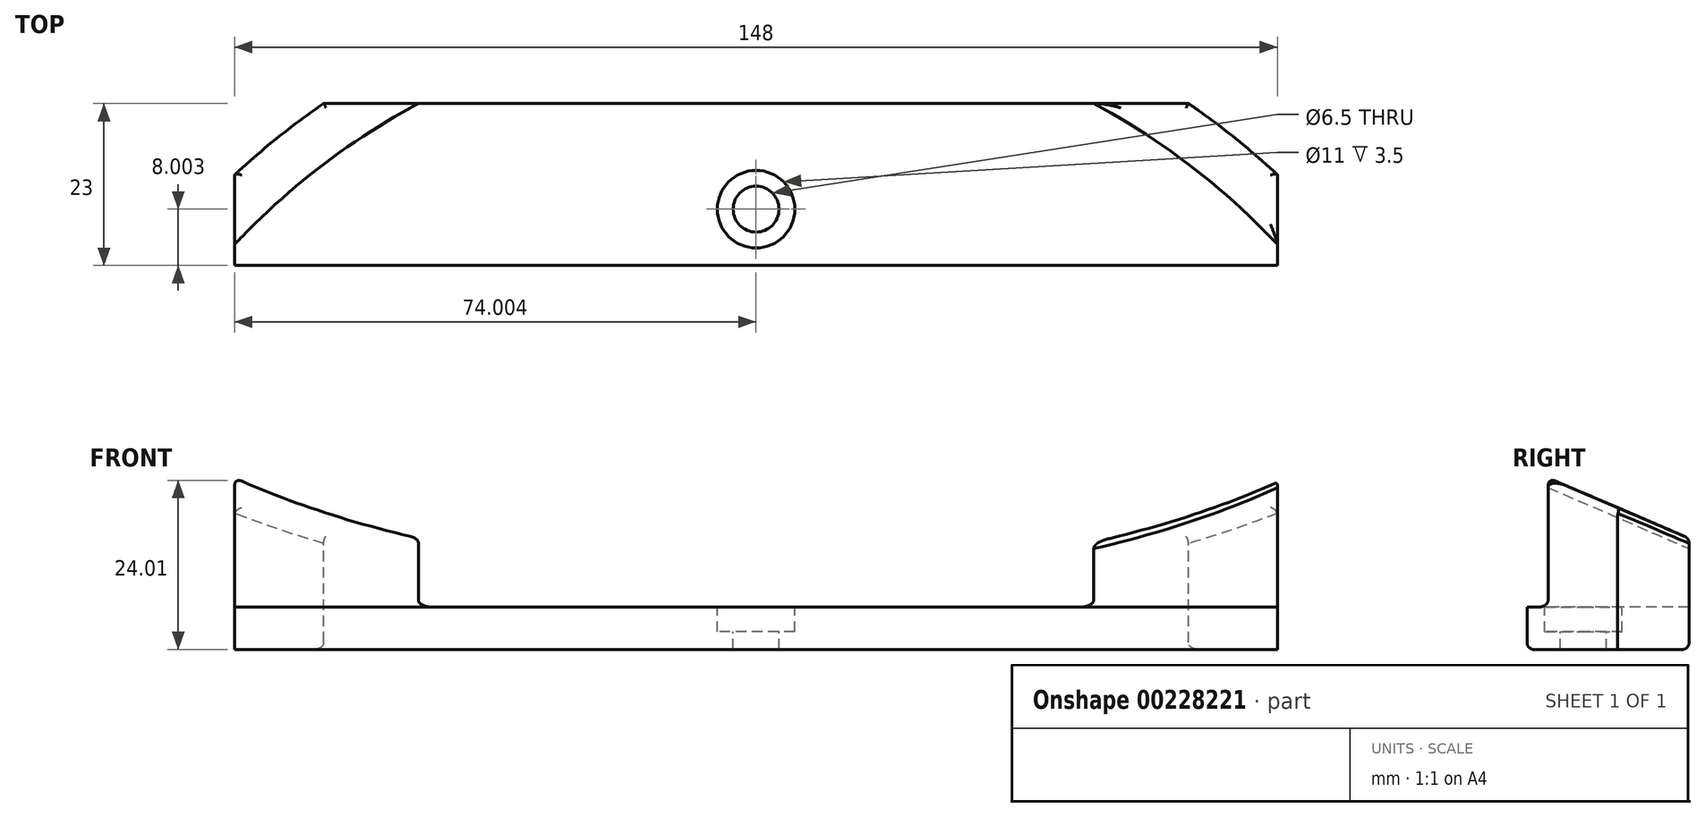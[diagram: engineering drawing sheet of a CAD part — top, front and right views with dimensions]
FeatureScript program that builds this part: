
annotation { "Feature Type Name" : "Feature", "Feature Type Description" : "" }
export const myFeature = defineFeature(function(context is Context, id is Id, definition is map)
    precondition{}
    {
        {
            var Q0;
            Q0=qCreatedBy(makeId("Top.planeOp"),FACE);
            var sketch = newSketch(context, id + "F0", { "sketchPlane" : qUnion([Q0])});
            skLineSegment(sketch, "E0.bottom", {"start": v(-72.48, -7.14) * mm, "end": v(107.52, -7.14) * mm});
            skLineSegment(sketch, "E0.top", {"start": v(-72.48, -30.14) * mm, "end": v(107.52, -30.14) * mm});
            skLineSegment(sketch, "E0.left", {"start": v(-72.48, -7.14) * mm, "end": v(-72.48, -30.14) * mm});
            skLineSegment(sketch, "E0.right", {"start": v(107.52, -7.14) * mm, "end": v(107.52, -30.14) * mm});
            skPoint(sketch, "E1", {"position": v(-64.48, -22.14) * mm});
            skPoint(sketch, "E2", {"position": v(99.52, -22.14) * mm});
            skSolve(sketch);
        }
        {
            var Q0;
            Q0=makeQuery(id+"F0.imprint","IMPRINT",FACE,{"disambiguationData":[TD([[makeQuery(id+"F0.imprint","IMPRINT",EDGE,{"derivedFrom":sQuery(id+"F0.wireOp",EDGE,"E0.bottom")}),-1.0]])]});
            extrude(context, id + "F1", {"entities" : qUnion([Q0]), "depth" : 6 * mm});
        }
        {
            var Q0;
            Q0=makeQuery(id+"F1.opExtrude","CAP_FACE",FACE,{"disambiguationData":[OSD([sQuery(id+"F0.wireOp",EDGE,"E0.bottom"),sQuery(id+"F0.wireOp",EDGE,"E0.top"),sQuery(id+"F0.wireOp",EDGE,"E0.left"),sQuery(id+"F0.wireOp",EDGE,"E0.right")])],"isStart":false});
            var sketch = newSketch(context, id + "F2", { "sketchPlane" : qUnion([Q0])});
            skPoint(sketch, "E3", {"position": v(-64.48, -22.14) * mm});
            skPoint(sketch, "E4", {"position": v(99.52, -22.14) * mm});
            skLineSegment(sketch, "E5.bottom", {"start": v(-56.48, -7.14) * mm, "end": v(91.52, -7.14) * mm});
            skLineSegment(sketch, "E5.top", {"start": v(-56.48, -30.14) * mm, "end": v(91.52, -30.14) * mm});
            skLineSegment(sketch, "E5.left", {"start": v(-56.48, -7.14) * mm, "end": v(-56.48, -30.14) * mm});
            skLineSegment(sketch, "E5.right", {"start": v(91.52, -7.14) * mm, "end": v(91.52, -30.14) * mm});
            skSolve(sketch);
        }
        {
            var Q0;
            Q0=makeQuery(id+"F2.imprint","IMPRINT",FACE,{"disambiguationData":[TD([[makeQuery(id+"F2.imprint","IMPRINT",EDGE,{"derivedFrom":sQuery(id+"F2.wireOp",EDGE,"E5.bottom")}),-1.0]])]});
            extrude(context, id + "F3", {"entities" : qUnion([Q0]), "operationType" : NewBodyOperationType.ADD, "depth" : 21 * mm});
        }
        {
            var Q0;
            Q0=makeQuery(id+"F3.opExtrude","CAP_FACE",FACE,{"disambiguationData":[OSD([sQuery(id+"F2.wireOp",EDGE,"E5.bottom"),sQuery(id+"F2.wireOp",EDGE,"E5.top"),sQuery(id+"F2.wireOp",EDGE,"E5.left"),sQuery(id+"F2.wireOp",EDGE,"E5.right")])],"isStart":false});
            var sketch = newSketch(context, id + "F4", { "sketchPlane" : qUnion([Q0])});
            skPoint(sketch, "E6", {"position": v(17.52, 2.86) * mm});
            skCircle(sketch, "E7", {"center": v(17.52, -96.6) * mm, "radius": 108.5 * mm});
            skCircle(sketch, "E8", {"center": v(17.52, -96.6) * mm, "radius": 101.5 * mm});
            skSolve(sketch);
        }
        {
            var Q0;
            {var subQ1=makeQuery(id+"F3.opExtrude","CAP_EDGE",EDGE,{"disambiguationData":[OSD([sQuery(id+"F2.wireOp",EDGE,"E5.top")])],"isStart":false});Q0=makeQuery(id+"F4.imprint","IMPRINT",FACE,{"disambiguationData":[TD([[makeQuery(id+"F4.imprint","IMPRINT",EDGE,{"derivedFrom":subQ1}),1.0]])]});}
            extrude(context, id + "F5", {"entities" : qUnion([Q0]), "operationType" : NewBodyOperationType.REMOVE, "oppositeDirection" : true, "depth" : 21 * mm});
        }
        {
            var Q0;
            {var subQ0=sQuery(id+"F4.wireOp",EDGE,"E7");var subQ1=makeQuery(id+"F3.opExtrude","CAP_EDGE",EDGE,{"disambiguationData":[OSD([sQuery(id+"F2.wireOp",EDGE,"E5.bottom")])],"isStart":false});var subQ2=makeQuery(id+"F4.imprint","INTERSECT",VERTEX,{"disambiguationData":[OD(1.0)],"derivedFrom":[subQ1,subQ0]});Q0=makeQuery(id+"F4.imprint","IMPRINT",FACE,{"disambiguationData":[TD([[makeQuery(id+"F4.imprint","IMPRINT",EDGE,{"disambiguationData":[TD([[subQ2,-1.0]])],"derivedFrom":subQ0}),-1.0]])]});}
            var Q1;
            {var subQ0=sQuery(id+"F4.wireOp",EDGE,"E7");var subQ1=makeQuery(id+"F3.opExtrude","CAP_EDGE",EDGE,{"disambiguationData":[OSD([sQuery(id+"F2.wireOp",EDGE,"E5.bottom")])],"isStart":false});var subQ2=makeQuery(id+"F4.imprint","INTERSECT",VERTEX,{"disambiguationData":[OD(0.0)],"derivedFrom":[subQ1,subQ0]});Q1=makeQuery(id+"F4.imprint","IMPRINT",FACE,{"disambiguationData":[TD([[makeQuery(id+"F4.imprint","IMPRINT",EDGE,{"disambiguationData":[TD([[subQ2,1.0]])],"derivedFrom":subQ0}),-1.0]])]});}
            extrude(context, id + "F6", {"entities" : qUnion([Q0, Q1]), "operationType" : NewBodyOperationType.REMOVE, "oppositeDirection" : true, "depth" : 35 * mm});
        }
        {
            var Q0;
            Q0=makeQuery(id+"F1.opExtrude","SWEPT_FACE",FACE,{"disambiguationData":[OSD([sQuery(id+"F0.wireOp",EDGE,"E0.right")])]});
            var sketch = newSketch(context, id + "F7", { "sketchPlane" : qUnion([Q0])});
            skLineSegment(sketch, "E9", {"start": v(-33.26, 27) * mm, "end": v(-1.82, 13.5) * mm});
            skLineSegment(sketch, "E10", {"start": v(-1.82, 13.5) * mm, "end": v(-1.82, 27.27) * mm});
            skLineSegment(sketch, "E11", {"start": v(-1.82, 27.27) * mm, "end": v(-33.26, 27) * mm});
            skSolve(sketch);
        }
        {
            var Q0;
            Q0=makeQuery(id+"F7.imprint","IMPRINT",FACE,{"disambiguationData":[TD([[makeQuery(id+"F7.imprint","IMPRINT",EDGE,{"derivedFrom":sQuery(id+"F7.wireOp",EDGE,"E9")}),1.0]])]});
            extrude(context, id + "F8", {"entities" : qUnion([Q0]), "operationType" : NewBodyOperationType.REMOVE, "oppositeDirection" : true, "depth" : 200 * mm});
        }
        {
            var Q0;
            {var subQ0=sQuery(id+"F2.wireOp",EDGE,"E5.left");Q0=makeQuery(id+"F2.imprint","IMPRINT",FACE,{"disambiguationData":[TD([[makeQuery(id+"F2.imprint","IMPRINT",EDGE,{"derivedFrom":subQ0}),-1.0]])]});}
            var Q1;
            {var subQ0=sQuery(id+"F2.wireOp",EDGE,"E5.right");Q1=makeQuery(id+"F2.imprint","IMPRINT",FACE,{"disambiguationData":[TD([[makeQuery(id+"F2.imprint","IMPRINT",EDGE,{"derivedFrom":subQ0}),1.0]])]});}
            extrude(context, id + "F9", {"entities" : qUnion([Q0, Q1]), "operationType" : NewBodyOperationType.REMOVE, "oppositeDirection" : true, "depth" : 25 * mm});
        }
        {
            var Q0;
            {var subQ0=sQuery(id+"F2.wireOp",EDGE,"E5.right");var subQ1=sQuery(id+"F2.wireOp",EDGE,"E5.left");var subQ2=sQuery(id+"F2.wireOp",EDGE,"E5.top");var subQ3=sQuery(id+"F2.wireOp",EDGE,"E5.bottom");var subQ4=sQuery(id+"F0.wireOp",EDGE,"E0.right");var subQ6=sQuery(id+"F0.wireOp",EDGE,"E0.top");var subQ8=sQuery(id+"F0.wireOp",EDGE,"E0.bottom");var subQ11=sQuery(id+"F0.wireOp",EDGE,"E0.left");var subQ12=makeQuery(id+"F1.opExtrude","CAP_FACE",FACE,{"disambiguationData":[OSD([subQ8,subQ6,subQ11,subQ4])],"isStart":false});Q0=makeQuery(id+"F5.boolean.opBoolean","MERGE",FACE,{"derivedFrom":[makeQuery(id+"F3.boolean.opBoolean","SPLIT",FACE,{"disambiguationData":[TD([makeQuery(id+"F1.opExtrude","SWEPT_FACE",FACE,{"disambiguationData":[OSD([subQ11])]})])],"derivedFrom":subQ12}),makeQuery(id+"F3.boolean.opBoolean","SPLIT",FACE,{"disambiguationData":[TD([makeQuery(id+"F1.opExtrude","SWEPT_FACE",FACE,{"disambiguationData":[OSD([subQ4])]})])],"derivedFrom":subQ12}),makeQuery(id+"F5.opExtrude","CAP_FACE",FACE,{"disambiguationData":[OSD([subQ3,subQ2,subQ1,subQ0,sQuery(id+"F4.wireOp",EDGE,"E8")])],"isStart":false})]});}
            var sketch = newSketch(context, id + "F10", { "sketchPlane" : qUnion([Q0])});
            skPoint(sketch, "E12", {"position": v(17.52, -22.14) * mm});
            skSolve(sketch);
        }
        {
            var Q0;
            Q0=sQuery(id+"F10.wireOp",VERTEX,"E12");
            var Q1;
            Q1=makeQuery(id+"F1.opExtrude","SWEPT_BODY",BODY,{"disambiguationData":[OSD([sQuery(id+"F0.wireOp",EDGE,"E0.bottom"),sQuery(id+"F0.wireOp",EDGE,"E0.top"),sQuery(id+"F0.wireOp",EDGE,"E0.left"),sQuery(id+"F0.wireOp",EDGE,"E0.right")])]});
            hole(context, id + "F11", {"style" : HoleStyle.C_BORE, "endStyle" : HoleEndStyle.THROUGH, "holeDiameter" : 6.5 * mm, "cBoreDiameter" : 11 * mm, "cBoreDepth" : 3.5 * mm, "startFromSketch" : true, "locations" : qUnion([Q0]), "scope" : qUnion([Q1]), "isTappedThrough" : true});
        }
        {
            var Q0;
            Q0=makeQuery(id+"F5.boolean.opBoolean","COPY",EDGE,{"derivedFrom":makeQuery(id+"F5.opExtrude","CAP_EDGE",EDGE,{"disambiguationData":[OSD([sQuery(id+"F2.wireOp",EDGE,"E5.bottom")])],"isStart":false})});
            var Q1;
            Q1=makeQuery(id+"F5.boolean.opBoolean","COPY",EDGE,{"derivedFrom":makeQuery(id+"F5.opExtrude","CAP_EDGE",EDGE,{"disambiguationData":[OSD([sQuery(id+"F2.wireOp",EDGE,"E5.top")])],"isStart":false})});
            var Q2;
            {var subQ0=sQuery(id+"F4.wireOp",EDGE,"E7");var subQ1=sQuery(id+"F2.wireOp",EDGE,"E5.bottom");var subQ2=makeQuery(id+"F3.opExtrude","CAP_EDGE",EDGE,{"disambiguationData":[OSD([subQ1])],"isStart":false});var subQ3=sQuery(id+"F0.wireOp",EDGE,"E0.bottom");Q2=makeQuery(id+"F6.boolean.opBoolean","SPLIT",EDGE,{"disambiguationData":[TD([makeQuery(id+"F6.opExtrude","SWEPT_FACE",FACE,{"disambiguationData":[OSD([subQ0]),TDD([makeQuery(id+"F4.imprint","IMPRINT",EDGE,{"disambiguationData":[TD([[makeQuery(id+"F4.imprint","INTERSECT",VERTEX,{"disambiguationData":[OD(0.0)],"derivedFrom":[subQ2,subQ0]}),1.0]])],"derivedFrom":subQ0})])]})])],"derivedFrom":makeQuery(id+"F1.opExtrude","CAP_EDGE",EDGE,{"disambiguationData":[OSD([subQ3])],"isStart":true})});}
            var Q3;
            Q3=makeQuery(id+"F1.opExtrude","CAP_EDGE",EDGE,{"disambiguationData":[OSD([sQuery(id+"F0.wireOp",EDGE,"E0.top")])],"isStart":true});
            var Q4;
            {var subQ0=sQuery(id+"F4.wireOp",EDGE,"E7");var subQ1=sQuery(id+"F2.wireOp",EDGE,"E5.bottom");var subQ2=sQuery(id+"F2.wireOp",EDGE,"E5.left");var subQ6=sQuery(id+"F0.wireOp",EDGE,"E0.right");var subQ7=sQuery(id+"F0.wireOp",EDGE,"E0.left");var subQ8=sQuery(id+"F0.wireOp",EDGE,"E0.top");var subQ9=sQuery(id+"F0.wireOp",EDGE,"E0.bottom");var subQ11=makeQuery(id+"F6.opExtrude","SWEPT_EDGE",EDGE,{"disambiguationData":[OSD([subQ2,subQ0])]});Q4=makeQuery(id+"F9.boolean.opBoolean","MERGE",EDGE,{"derivedFrom":[makeQuery(id+"F6.boolean.opBoolean","COPY",EDGE,{"disambiguationData":[TD([makeQuery(id+"F1.opExtrude","CAP_FACE",FACE,{"disambiguationData":[OSD([subQ9,subQ8,subQ7,subQ6])],"isStart":true})])],"derivedFrom":subQ11}),makeQuery(id+"F6.boolean.opBoolean","COPY",EDGE,{"disambiguationData":[TD([makeQuery(id+"F3.opExtrude","CAP_FACE",FACE,{"disambiguationData":[OSD([subQ1,sQuery(id+"F2.wireOp",EDGE,"E5.top"),subQ2,sQuery(id+"F2.wireOp",EDGE,"E5.right")])],"isStart":false})])],"derivedFrom":subQ11})]});}
            var Q5;
            {var subQ0=sQuery(id+"F4.wireOp",EDGE,"E7");var subQ1=sQuery(id+"F2.wireOp",EDGE,"E5.bottom");Q5=makeQuery(id+"F6.boolean.opBoolean","COPY",EDGE,{"derivedFrom":makeQuery(id+"F6.opExtrude","SWEPT_EDGE",EDGE,{"disambiguationData":[OSD([subQ1,subQ0]),TDD([makeQuery(id+"F4.imprint","INTERSECT",VERTEX,{"disambiguationData":[OD(1.0)],"derivedFrom":[makeQuery(id+"F3.opExtrude","CAP_EDGE",EDGE,{"disambiguationData":[OSD([subQ1])],"isStart":false}),subQ0]})])]})});}
            var Q6;
            {var subQ0=sQuery(id+"F4.wireOp",EDGE,"E7");var subQ1=sQuery(id+"F2.wireOp",EDGE,"E5.bottom");var subQ2=sQuery(id+"F2.wireOp",EDGE,"E5.right");var subQ5=sQuery(id+"F0.wireOp",EDGE,"E0.right");var subQ6=sQuery(id+"F0.wireOp",EDGE,"E0.left");var subQ7=sQuery(id+"F0.wireOp",EDGE,"E0.top");var subQ8=sQuery(id+"F0.wireOp",EDGE,"E0.bottom");var subQ11=makeQuery(id+"F6.opExtrude","SWEPT_EDGE",EDGE,{"disambiguationData":[OSD([subQ2,subQ0])]});Q6=makeQuery(id+"F9.boolean.opBoolean","MERGE",EDGE,{"derivedFrom":[makeQuery(id+"F6.boolean.opBoolean","COPY",EDGE,{"disambiguationData":[TD([makeQuery(id+"F1.opExtrude","CAP_FACE",FACE,{"disambiguationData":[OSD([subQ8,subQ7,subQ6,subQ5])],"isStart":true})])],"derivedFrom":subQ11}),makeQuery(id+"F6.boolean.opBoolean","COPY",EDGE,{"disambiguationData":[TD([makeQuery(id+"F3.opExtrude","CAP_FACE",FACE,{"disambiguationData":[OSD([subQ1,sQuery(id+"F2.wireOp",EDGE,"E5.top"),sQuery(id+"F2.wireOp",EDGE,"E5.left"),subQ2])],"isStart":false})])],"derivedFrom":subQ11})]});}
            var Q7;
            {var subQ0=sQuery(id+"F4.wireOp",EDGE,"E8");Q7=makeQuery(id+"F8.boolean.opBoolean","INTERSECT",EDGE,{"derivedFrom":[makeQuery(id+"F5.boolean.opBoolean","COPY",FACE,{"derivedFrom":makeQuery(id+"F5.opExtrude","SWEPT_FACE",FACE,{"disambiguationData":[OSD([subQ0]),TDD([makeQuery(id+"F4.imprint","IMPRINT",EDGE,{"disambiguationData":[TD([[makeQuery(id+"F4.imprint","INTERSECT",VERTEX,{"disambiguationData":[OD(0.0)],"derivedFrom":[makeQuery(id+"F3.opExtrude","CAP_EDGE",EDGE,{"disambiguationData":[OSD([sQuery(id+"F2.wireOp",EDGE,"E5.bottom")])],"isStart":false}),subQ0]}),1.0]])],"derivedFrom":subQ0})])]})}),makeQuery(id+"F8.opExtrude","SWEPT_FACE",FACE,{"disambiguationData":[OSD([sQuery(id+"F7.wireOp",EDGE,"E9")])]})]});}
            var Q8;
            {var subQ0=sQuery(id+"F4.wireOp",EDGE,"E7");Q8=makeQuery(id+"F8.boolean.opBoolean","INTERSECT",EDGE,{"derivedFrom":[makeQuery(id+"F6.boolean.opBoolean","COPY",FACE,{"derivedFrom":makeQuery(id+"F6.opExtrude","SWEPT_FACE",FACE,{"disambiguationData":[OSD([subQ0]),TDD([makeQuery(id+"F4.imprint","IMPRINT",EDGE,{"disambiguationData":[TD([[makeQuery(id+"F4.imprint","INTERSECT",VERTEX,{"disambiguationData":[OD(0.0)],"derivedFrom":[makeQuery(id+"F3.opExtrude","CAP_EDGE",EDGE,{"disambiguationData":[OSD([sQuery(id+"F2.wireOp",EDGE,"E5.bottom")])],"isStart":false}),subQ0]}),1.0]])],"derivedFrom":subQ0})])]})}),makeQuery(id+"F8.opExtrude","SWEPT_FACE",FACE,{"disambiguationData":[OSD([sQuery(id+"F7.wireOp",EDGE,"E9")])]})]});}
            var Q9;
            {var subQ0=sQuery(id+"F4.wireOp",EDGE,"E8");var subQ4=sQuery(id+"F2.wireOp",EDGE,"E5.bottom");var subQ5=makeQuery(id+"F3.opExtrude","CAP_EDGE",EDGE,{"disambiguationData":[OSD([subQ4])],"isStart":false});var subQ9=sQuery(id+"F0.wireOp",EDGE,"E0.bottom");Q9=makeQuery(id+"F8.boolean.opBoolean","INTERSECT",EDGE,{"disambiguationData":[OD(0.0)],"derivedFrom":[makeQuery(id+"F6.boolean.opBoolean","SPLIT",FACE,{"disambiguationData":[TD([makeQuery(id+"F5.boolean.opBoolean","COPY",FACE,{"derivedFrom":makeQuery(id+"F5.opExtrude","SWEPT_FACE",FACE,{"disambiguationData":[OSD([subQ0]),TDD([makeQuery(id+"F4.imprint","IMPRINT",EDGE,{"disambiguationData":[TD([[makeQuery(id+"F4.imprint","INTERSECT",VERTEX,{"disambiguationData":[OD(0.0)],"derivedFrom":[subQ5,subQ0]}),1.0]])],"derivedFrom":subQ0})])]})})])],"derivedFrom":makeQuery(id+"F3.boolean.opBoolean","MERGE",FACE,{"derivedFrom":[makeQuery(id+"F1.opExtrude","SWEPT_FACE",FACE,{"disambiguationData":[OSD([subQ9])]}),makeQuery(id+"F3.opExtrude","SWEPT_FACE",FACE,{"disambiguationData":[OSD([subQ4])]})]})}),makeQuery(id+"F8.opExtrude","SWEPT_FACE",FACE,{"disambiguationData":[OSD([sQuery(id+"F7.wireOp",EDGE,"E9")])]})]});}
            var Q10;
            Q10=makeQuery(id+"F8.boolean.opBoolean","INTERSECT",EDGE,{"derivedFrom":[makeQuery(id+"F3.opExtrude","SWEPT_FACE",FACE,{"disambiguationData":[OSD([sQuery(id+"F2.wireOp",EDGE,"E5.right")])]}),makeQuery(id+"F8.opExtrude","SWEPT_FACE",FACE,{"disambiguationData":[OSD([sQuery(id+"F7.wireOp",EDGE,"E9")])]})]});
            var Q11;
            {var subQ0=sQuery(id+"F4.wireOp",EDGE,"E7");Q11=makeQuery(id+"F8.boolean.opBoolean","INTERSECT",EDGE,{"derivedFrom":[makeQuery(id+"F6.boolean.opBoolean","COPY",FACE,{"derivedFrom":makeQuery(id+"F6.opExtrude","SWEPT_FACE",FACE,{"disambiguationData":[OSD([subQ0]),TDD([makeQuery(id+"F4.imprint","IMPRINT",EDGE,{"disambiguationData":[TD([[makeQuery(id+"F4.imprint","INTERSECT",VERTEX,{"disambiguationData":[OD(1.0)],"derivedFrom":[makeQuery(id+"F3.opExtrude","CAP_EDGE",EDGE,{"disambiguationData":[OSD([sQuery(id+"F2.wireOp",EDGE,"E5.bottom")])],"isStart":false}),subQ0]}),-1.0]])],"derivedFrom":subQ0})])]})}),makeQuery(id+"F8.opExtrude","SWEPT_FACE",FACE,{"disambiguationData":[OSD([sQuery(id+"F7.wireOp",EDGE,"E9")])]})]});}
            var Q12;
            {var subQ0=sQuery(id+"F4.wireOp",EDGE,"E8");var subQ4=sQuery(id+"F2.wireOp",EDGE,"E5.bottom");var subQ5=makeQuery(id+"F3.opExtrude","CAP_EDGE",EDGE,{"disambiguationData":[OSD([subQ4])],"isStart":false});var subQ9=sQuery(id+"F0.wireOp",EDGE,"E0.bottom");Q12=makeQuery(id+"F8.boolean.opBoolean","INTERSECT",EDGE,{"disambiguationData":[OD(1.0)],"derivedFrom":[makeQuery(id+"F6.boolean.opBoolean","SPLIT",FACE,{"disambiguationData":[TD([makeQuery(id+"F5.boolean.opBoolean","COPY",FACE,{"derivedFrom":makeQuery(id+"F5.opExtrude","SWEPT_FACE",FACE,{"disambiguationData":[OSD([subQ0]),TDD([makeQuery(id+"F4.imprint","IMPRINT",EDGE,{"disambiguationData":[TD([[makeQuery(id+"F4.imprint","INTERSECT",VERTEX,{"disambiguationData":[OD(0.0)],"derivedFrom":[subQ5,subQ0]}),1.0]])],"derivedFrom":subQ0})])]})})])],"derivedFrom":makeQuery(id+"F3.boolean.opBoolean","MERGE",FACE,{"derivedFrom":[makeQuery(id+"F1.opExtrude","SWEPT_FACE",FACE,{"disambiguationData":[OSD([subQ9])]}),makeQuery(id+"F3.opExtrude","SWEPT_FACE",FACE,{"disambiguationData":[OSD([subQ4])]})]})}),makeQuery(id+"F8.opExtrude","SWEPT_FACE",FACE,{"disambiguationData":[OSD([sQuery(id+"F7.wireOp",EDGE,"E9")])]})]});}
            var Q13;
            Q13=makeQuery(id+"F8.boolean.opBoolean","INTERSECT",EDGE,{"derivedFrom":[makeQuery(id+"F3.opExtrude","SWEPT_FACE",FACE,{"disambiguationData":[OSD([sQuery(id+"F2.wireOp",EDGE,"E5.left")])]}),makeQuery(id+"F8.opExtrude","SWEPT_FACE",FACE,{"disambiguationData":[OSD([sQuery(id+"F7.wireOp",EDGE,"E9")])]})]});
            var Q14;
            {var subQ0=sQuery(id+"F4.wireOp",EDGE,"E8");var subQ1=sQuery(id+"F2.wireOp",EDGE,"E5.bottom");Q14=makeQuery(id+"F5.boolean.opBoolean","COPY",EDGE,{"derivedFrom":makeQuery(id+"F5.opExtrude","SWEPT_EDGE",EDGE,{"disambiguationData":[OSD([subQ1,subQ0]),TDD([makeQuery(id+"F4.imprint","INTERSECT",VERTEX,{"disambiguationData":[OD(0.0)],"derivedFrom":[makeQuery(id+"F3.opExtrude","CAP_EDGE",EDGE,{"disambiguationData":[OSD([subQ1])],"isStart":false}),subQ0]})])]})});}
            var Q15;
            {var subQ0=sQuery(id+"F4.wireOp",EDGE,"E8");var subQ1=sQuery(id+"F2.wireOp",EDGE,"E5.bottom");Q15=makeQuery(id+"F5.boolean.opBoolean","COPY",EDGE,{"derivedFrom":makeQuery(id+"F5.opExtrude","SWEPT_EDGE",EDGE,{"disambiguationData":[OSD([subQ1,subQ0]),TDD([makeQuery(id+"F4.imprint","INTERSECT",VERTEX,{"disambiguationData":[OD(1.0)],"derivedFrom":[makeQuery(id+"F3.opExtrude","CAP_EDGE",EDGE,{"disambiguationData":[OSD([subQ1])],"isStart":false}),subQ0]})])]})});}
            var Q16;
            {var subQ0=sQuery(id+"F4.wireOp",EDGE,"E8");Q16=makeQuery(id+"F5.boolean.opBoolean","COPY",EDGE,{"derivedFrom":makeQuery(id+"F5.opExtrude","CAP_EDGE",EDGE,{"disambiguationData":[OSD([subQ0]),TDD([makeQuery(id+"F4.imprint","IMPRINT",EDGE,{"disambiguationData":[TD([[makeQuery(id+"F4.imprint","INTERSECT",VERTEX,{"disambiguationData":[OD(0.0)],"derivedFrom":[makeQuery(id+"F3.opExtrude","CAP_EDGE",EDGE,{"disambiguationData":[OSD([sQuery(id+"F2.wireOp",EDGE,"E5.bottom")])],"isStart":false}),subQ0]}),1.0]])],"derivedFrom":subQ0})])],"isStart":false})});}
            var Q17;
            {var subQ0=sQuery(id+"F4.wireOp",EDGE,"E8");Q17=makeQuery(id+"F5.boolean.opBoolean","COPY",EDGE,{"derivedFrom":makeQuery(id+"F5.opExtrude","CAP_EDGE",EDGE,{"disambiguationData":[OSD([subQ0]),TDD([makeQuery(id+"F4.imprint","IMPRINT",EDGE,{"disambiguationData":[TD([[makeQuery(id+"F4.imprint","INTERSECT",VERTEX,{"disambiguationData":[OD(1.0)],"derivedFrom":[makeQuery(id+"F3.opExtrude","CAP_EDGE",EDGE,{"disambiguationData":[OSD([sQuery(id+"F2.wireOp",EDGE,"E5.bottom")])],"isStart":false}),subQ0]}),-1.0]])],"derivedFrom":subQ0})])],"isStart":false})});}
            var Q18;
            {var subQ0=sQuery(id+"F4.wireOp",EDGE,"E7");var subQ1=sQuery(id+"F2.wireOp",EDGE,"E5.bottom");Q18=makeQuery(id+"F6.boolean.opBoolean","COPY",EDGE,{"derivedFrom":makeQuery(id+"F6.opExtrude","SWEPT_EDGE",EDGE,{"disambiguationData":[OSD([subQ1,subQ0]),TDD([makeQuery(id+"F4.imprint","INTERSECT",VERTEX,{"disambiguationData":[OD(0.0)],"derivedFrom":[makeQuery(id+"F3.opExtrude","CAP_EDGE",EDGE,{"disambiguationData":[OSD([subQ1])],"isStart":false}),subQ0]})])]})});}
            var Q19;
            Q19=makeQuery(id+"F11.hole-0.boolean.opBoolean","COPY",EDGE,{"derivedFrom":makeQuery(id+"F11.hole-0.opRevolve","SWEPT_EDGE",EDGE,{"disambiguationData":[OSD([sQuery(id+"F11.hole-0.sketch.wireOp",EDGE,"cbore_start_line_1"),sQuery(id+"F11.hole-0.sketch.wireOp",EDGE,"core_line_2")])]})});
            var Q20;
            Q20=makeQuery(id+"F11.hole-0.boolean.opBoolean","COPY",EDGE,{"derivedFrom":makeQuery(id+"F11.hole-0.opRevolve","SWEPT_EDGE",EDGE,{"disambiguationData":[OSD([sQuery(id+"F11.hole-0.sketch.wireOp",EDGE,"cbore_start_line_2"),sQuery(id+"F11.hole-0.sketch.wireOp",EDGE,"cbore_start_line_3")])]})});
            fillet(context, id + "F12", {"entities" : qUnion([Q0, Q1, Q2, Q3, Q4, Q5, Q6, Q7, Q8, Q9, Q10, Q11, Q12, Q13, Q14, Q15, Q16, Q17, Q18, Q19, Q20]), "radius" : 1 * mm, "tangentPropagation" : true, "allowEdgeOverflow" : false});
        }
    });
